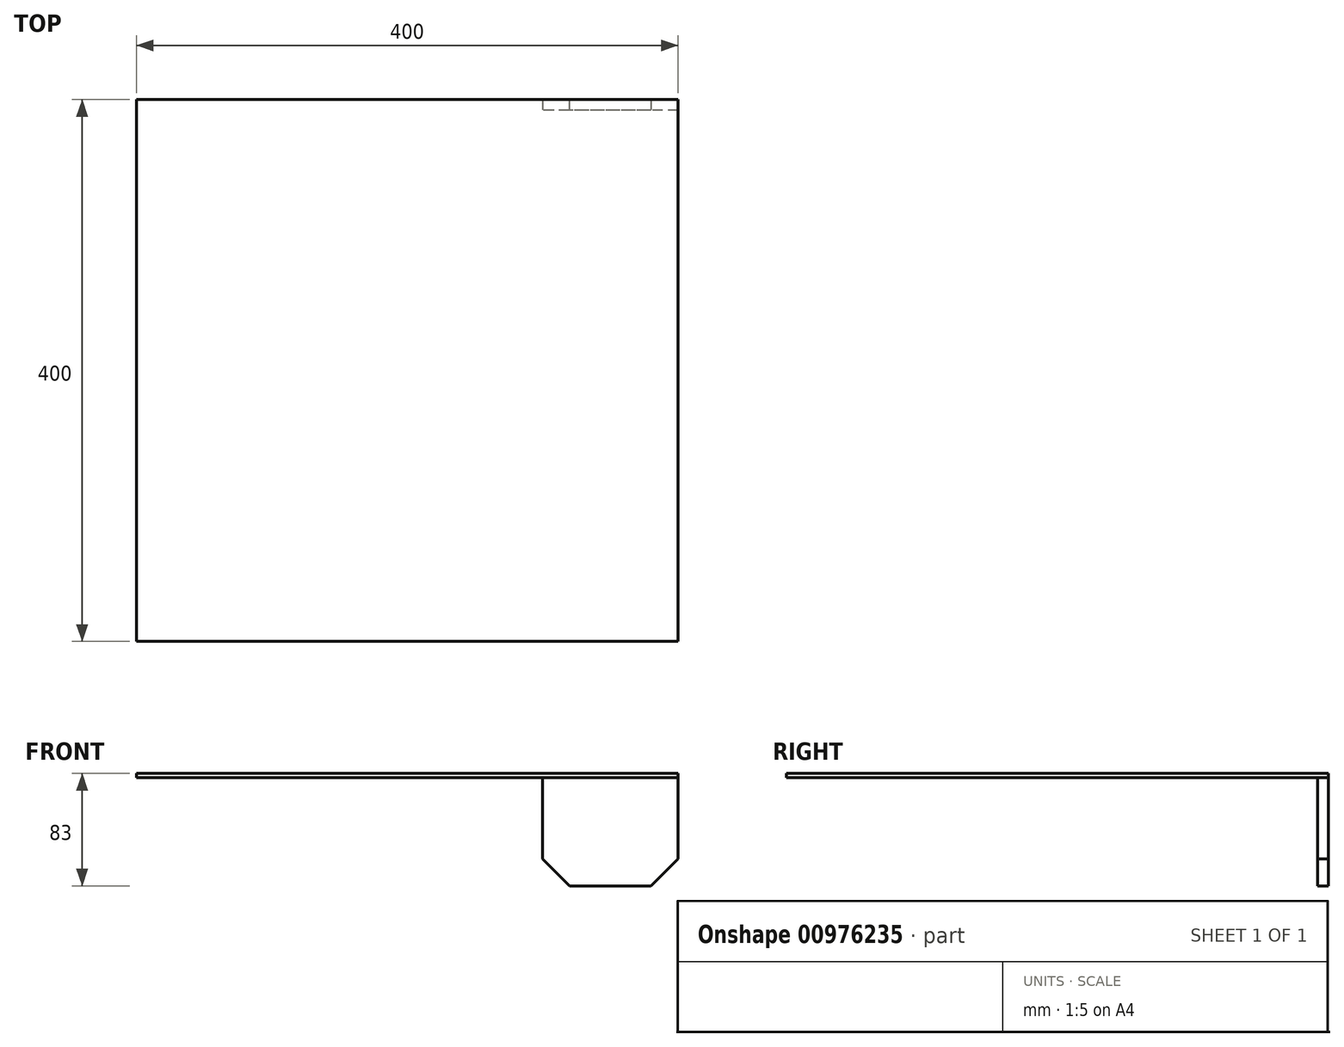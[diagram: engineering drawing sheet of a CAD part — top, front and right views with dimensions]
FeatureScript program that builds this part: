
annotation { "Feature Type Name" : "Feature", "Feature Type Description" : "" }
export const myFeature = defineFeature(function(context is Context, id is Id, definition is map)
    precondition{}
    {
        {
            var Q0;
            Q0=qCreatedBy(makeId("Top.planeOp"),FACE);
            var sketch = newSketch(context, id + "F0", { "sketchPlane" : qUnion([Q0])});
            skLineSegment(sketch, "E0.bottom", {"start": v(200, -200) * mm, "end": v(-200, -200) * mm});
            skLineSegment(sketch, "E0.top", {"start": v(200, 200) * mm, "end": v(-200, 200) * mm});
            skLineSegment(sketch, "E0.left", {"start": v(200, -200) * mm, "end": v(200, 200) * mm});
            skLineSegment(sketch, "E0.right", {"start": v(-200, -200) * mm, "end": v(-200, 200) * mm});
            skPoint(sketch, "E0.middle", {"position": v(0, 0) * mm});
            skSolve(sketch);
        }
        {
            var Q0;
            Q0=makeQuery(id+"F0.imprint","IMPRINT",FACE,{"disambiguationData":[TD([[makeQuery(id+"F0.imprint","IMPRINT",EDGE,{"derivedFrom":sQuery(id+"F0.wireOp",EDGE,"E0.bottom")}),-1.0]])]});
            extrude(context, id + "F1", {"entities" : qUnion([Q0]), "depth" : 3 * mm, "offsetDistance" : 25 * mm});
        }
        {
            var Q0;
            Q0=makeQuery(id+"F1.opExtrude","CAP_FACE",FACE,{"disambiguationData":[OSD([sQuery(id+"F0.wireOp",EDGE,"E0.bottom"),sQuery(id+"F0.wireOp",EDGE,"E0.top"),sQuery(id+"F0.wireOp",EDGE,"E0.left"),sQuery(id+"F0.wireOp",EDGE,"E0.right")])],"isStart":true});
            var sketch = newSketch(context, id + "F2", { "sketchPlane" : qUnion([Q0])});
            skLineSegment(sketch, "E1.bottom", {"start": v(200, -200) * mm, "end": v(100, -200) * mm});
            skLineSegment(sketch, "E1.top", {"start": v(200, -192) * mm, "end": v(100, -192) * mm});
            skLineSegment(sketch, "E1.left", {"start": v(200, -200) * mm, "end": v(200, -192) * mm});
            skLineSegment(sketch, "E1.right", {"start": v(100, -200) * mm, "end": v(100, -192) * mm});
            skSolve(sketch);
        }
        {
            var Q0;
            Q0=makeQuery(id+"F2.imprint","IMPRINT",FACE,{"disambiguationData":[TD([[makeQuery(id+"F2.imprint","IMPRINT",EDGE,{"derivedFrom":sQuery(id+"F2.wireOp",EDGE,"E1.bottom")}),-1.0]])]});
            extrude(context, id + "F3", {"entities" : qUnion([Q0]), "depth" : 80 * mm, "offsetDistance" : 25 * mm});
        }
        {
            var Q0;
            Q0=makeQuery(id+"F3.opExtrude","CAP_EDGE",EDGE,{"disambiguationData":[OSD([sQuery(id+"F2.wireOp",EDGE,"E1.left")])],"isStart":false});
            chamfer(context, id + "F4", {"entities" : qUnion([Q0]), "width" : 20 * mm, "tangentPropagation" : true});
        }
        {
            var Q0;
            Q0=makeQuery(id+"F3.opExtrude","CAP_EDGE",EDGE,{"disambiguationData":[OSD([sQuery(id+"F2.wireOp",EDGE,"E1.right")])],"isStart":false});
            chamfer(context, id + "F5", {"entities" : qUnion([Q0]), "width" : 20 * mm, "tangentPropagation" : true});
        }
    });
